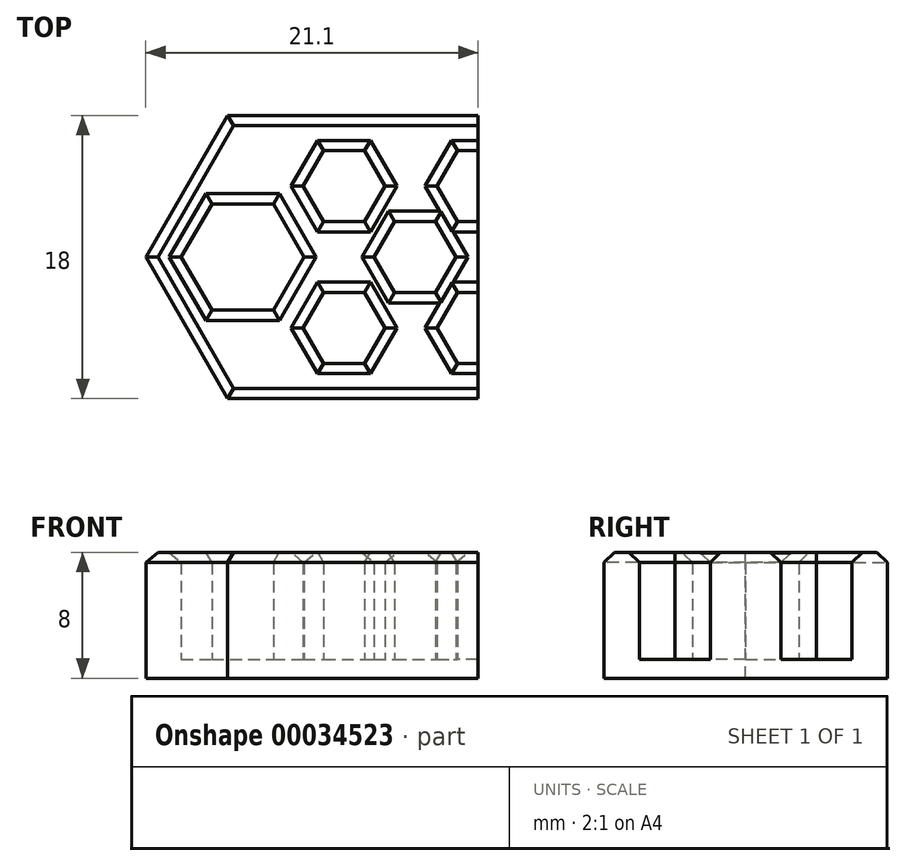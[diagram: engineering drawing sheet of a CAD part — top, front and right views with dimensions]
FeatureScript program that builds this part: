
annotation { "Feature Type Name" : "Feature", "Feature Type Description" : "" }
export const myFeature = defineFeature(function(context is Context, id is Id, definition is map)
    precondition{}
    {
        {
            assignVariable(context, id + "F0", {"name" : "d", "anyValue" : 4.5});
        }
        {
            var Q0;
            Q0=qCreatedBy(makeId("Top.planeOp"),FACE);
            var sketch = newSketch(context, id + "F1", { "sketchPlane" : qUnion([Q0])});
            skCircle(sketch, "E0.cCircle", {"center": v(0, 0) * mm, "radius": 2.25 * mm, "construction": true});
            skLineSegment(sketch, "E0.0", {"start": v(-1.3, 2.25) * mm, "end": v(1.3, 2.25) * mm});
            skLineSegment(sketch, "E0.1", {"start": v(1.3, 2.25) * mm, "end": v(2.6, 0) * mm});
            skLineSegment(sketch, "E0.2", {"start": v(2.6, 0) * mm, "end": v(1.3, -2.25) * mm});
            skLineSegment(sketch, "E0.3", {"start": v(1.3, -2.25) * mm, "end": v(-1.3, -2.25) * mm});
            skLineSegment(sketch, "E0.4", {"start": v(-1.3, -2.25) * mm, "end": v(-2.6, 0) * mm});
            skLineSegment(sketch, "E0.5", {"start": v(-2.6, 0) * mm, "end": v(-1.3, 2.25) * mm});
            skPoint(sketch, "E0.0.midPoint", {"position": v(0, 2.25) * mm});
            skCircle(sketch, "E1.cCircle", {"center": v(0, 9) * mm, "radius": 2.25 * mm, "construction": true});
            skLineSegment(sketch, "E1.0", {"start": v(-1.3, 11.25) * mm, "end": v(1.3, 11.25) * mm});
            skLineSegment(sketch, "E1.1", {"start": v(1.3, 11.25) * mm, "end": v(2.6, 9) * mm});
            skLineSegment(sketch, "E1.2", {"start": v(2.6, 9) * mm, "end": v(1.3, 6.75) * mm});
            skLineSegment(sketch, "E1.3", {"start": v(1.3, 6.75) * mm, "end": v(-1.3, 6.75) * mm});
            skLineSegment(sketch, "E1.4", {"start": v(-1.3, 6.75) * mm, "end": v(-2.6, 9) * mm});
            skLineSegment(sketch, "E1.5", {"start": v(-2.6, 9) * mm, "end": v(-1.3, 11.25) * mm});
            skPoint(sketch, "E1.0.midPoint", {"position": v(0, 11.25) * mm});
            skLineSegment(sketch, "E2", {"start": v(0, 0) * mm, "end": v(14.14, 14.14) * mm, "construction": true});
            skLineSegment(sketch, "E3", {"start": v(0, 2.25) * mm, "end": v(0, 6.75) * mm, "construction": true});
            skPoint(sketch, "E4", {"position": v(0, 4.5) * mm});
            skCircle(sketch, "E5.cCircle", {"center": v(4.5, 4.5) * mm, "radius": 2.25 * mm, "construction": true});
            skLineSegment(sketch, "E5.0", {"start": v(3.2, 6.75) * mm, "end": v(5.8, 6.75) * mm});
            skLineSegment(sketch, "E5.1", {"start": v(5.8, 6.75) * mm, "end": v(7.1, 4.5) * mm});
            skLineSegment(sketch, "E5.2", {"start": v(7.1, 4.5) * mm, "end": v(5.8, 2.25) * mm});
            skLineSegment(sketch, "E5.3", {"start": v(5.8, 2.25) * mm, "end": v(3.2, 2.25) * mm});
            skLineSegment(sketch, "E5.4", {"start": v(3.2, 2.25) * mm, "end": v(1.9, 4.5) * mm});
            skLineSegment(sketch, "E5.5", {"start": v(1.9, 4.5) * mm, "end": v(3.2, 6.75) * mm});
            skPoint(sketch, "E5.0.midPoint", {"position": v(4.5, 6.75) * mm});
            skCircle(sketch, "E6.1.0.0", {"center": v(13, 4.5) * mm, "radius": 2.25 * mm, "construction": true});
            skLineSegment(sketch, "E6.1.0.1", {"start": v(14.3, 6.75) * mm, "end": v(15.6, 4.5) * mm});
            skPoint(sketch, "E6.1.0.2", {"position": v(8.5, 2.25) * mm});
            skLineSegment(sketch, "E6.1.0.3", {"start": v(14.3, 2.25) * mm, "end": v(11.7, 2.25) * mm});
            skPoint(sketch, "E6.1.0.4", {"position": v(8.5, 11.25) * mm});
            skLineSegment(sketch, "E6.1.0.5", {"start": v(10.4, 4.5) * mm, "end": v(11.7, 6.75) * mm});
            skLineSegment(sketch, "E6.1.0.6", {"start": v(7.2, 6.75) * mm, "end": v(5.9, 9) * mm});
            skLineSegment(sketch, "E6.1.0.7", {"start": v(9.8, 6.75) * mm, "end": v(7.2, 6.75) * mm});
            skLineSegment(sketch, "E6.1.0.8", {"start": v(11.1, 9) * mm, "end": v(9.8, 6.75) * mm});
            skLineSegment(sketch, "E6.1.0.9", {"start": v(9.8, 11.25) * mm, "end": v(11.1, 9) * mm});
            skPoint(sketch, "E6.1.0.10", {"position": v(13, 6.75) * mm});
            skLineSegment(sketch, "E6.1.0.11", {"start": v(5.9, 9) * mm, "end": v(7.2, 11.25) * mm});
            skCircle(sketch, "E6.1.0.12", {"center": v(8.5, 9) * mm, "radius": 2.25 * mm, "construction": true});
            skLineSegment(sketch, "E6.1.0.13", {"start": v(15.6, 4.5) * mm, "end": v(14.3, 2.25) * mm});
            skLineSegment(sketch, "E6.1.0.14", {"start": v(11.7, 2.25) * mm, "end": v(10.4, 4.5) * mm});
            skLineSegment(sketch, "E6.1.0.15", {"start": v(5.9, 0) * mm, "end": v(7.2, 2.25) * mm});
            skLineSegment(sketch, "E6.1.0.16", {"start": v(7.2, -2.25) * mm, "end": v(5.9, 0) * mm});
            skLineSegment(sketch, "E6.1.0.17", {"start": v(9.8, -2.25) * mm, "end": v(7.2, -2.25) * mm});
            skLineSegment(sketch, "E6.1.0.18", {"start": v(11.1, 0) * mm, "end": v(9.8, -2.25) * mm});
            skLineSegment(sketch, "E6.1.0.19", {"start": v(9.8, 2.25) * mm, "end": v(11.1, 0) * mm});
            skCircle(sketch, "E6.1.0.20", {"center": v(8.5, 0) * mm, "radius": 2.25 * mm, "construction": true});
            skLineSegment(sketch, "E6.1.0.21", {"start": v(7.2, 11.25) * mm, "end": v(9.8, 11.25) * mm});
            skLineSegment(sketch, "E6.1.0.22", {"start": v(11.7, 6.75) * mm, "end": v(14.3, 6.75) * mm});
            skLineSegment(sketch, "E6.1.0.23", {"start": v(7.2, 2.25) * mm, "end": v(9.8, 2.25) * mm});
            skCircle(sketch, "E6.2.0.0", {"center": v(21.5, 4.5) * mm, "radius": 2.25 * mm, "construction": true});
            skLineSegment(sketch, "E6.2.0.1", {"start": v(22.8, 6.75) * mm, "end": v(24.1, 4.5) * mm});
            skPoint(sketch, "E6.2.0.2", {"position": v(17, 2.25) * mm});
            skLineSegment(sketch, "E6.2.0.3", {"start": v(22.8, 2.25) * mm, "end": v(20.2, 2.25) * mm});
            skPoint(sketch, "E6.2.0.4", {"position": v(17, 11.25) * mm});
            skLineSegment(sketch, "E6.2.0.5", {"start": v(18.9, 4.5) * mm, "end": v(20.2, 6.75) * mm});
            skLineSegment(sketch, "E6.2.0.6", {"start": v(15.7, 6.75) * mm, "end": v(14.4, 9) * mm});
            skLineSegment(sketch, "E6.2.0.7", {"start": v(18.3, 6.75) * mm, "end": v(15.7, 6.75) * mm});
            skLineSegment(sketch, "E6.2.0.8", {"start": v(19.6, 9) * mm, "end": v(18.3, 6.75) * mm});
            skLineSegment(sketch, "E6.2.0.9", {"start": v(18.3, 11.25) * mm, "end": v(19.6, 9) * mm});
            skPoint(sketch, "E6.2.0.10", {"position": v(21.5, 6.75) * mm});
            skLineSegment(sketch, "E6.2.0.11", {"start": v(14.4, 9) * mm, "end": v(15.7, 11.25) * mm});
            skCircle(sketch, "E6.2.0.12", {"center": v(17, 9) * mm, "radius": 2.25 * mm, "construction": true});
            skLineSegment(sketch, "E6.2.0.13", {"start": v(24.1, 4.5) * mm, "end": v(22.8, 2.25) * mm});
            skLineSegment(sketch, "E6.2.0.14", {"start": v(20.2, 2.25) * mm, "end": v(18.9, 4.5) * mm});
            skLineSegment(sketch, "E6.2.0.15", {"start": v(14.4, 0) * mm, "end": v(15.7, 2.25) * mm});
            skLineSegment(sketch, "E6.2.0.16", {"start": v(15.7, -2.25) * mm, "end": v(14.4, 0) * mm});
            skLineSegment(sketch, "E6.2.0.17", {"start": v(18.3, -2.25) * mm, "end": v(15.7, -2.25) * mm});
            skLineSegment(sketch, "E6.2.0.18", {"start": v(19.6, 0) * mm, "end": v(18.3, -2.25) * mm});
            skLineSegment(sketch, "E6.2.0.19", {"start": v(18.3, 2.25) * mm, "end": v(19.6, 0) * mm});
            skCircle(sketch, "E6.2.0.20", {"center": v(17, 0) * mm, "radius": 2.25 * mm, "construction": true});
            skLineSegment(sketch, "E6.2.0.21", {"start": v(15.7, 11.25) * mm, "end": v(18.3, 11.25) * mm});
            skLineSegment(sketch, "E6.2.0.22", {"start": v(20.2, 6.75) * mm, "end": v(22.8, 6.75) * mm});
            skLineSegment(sketch, "E6.2.0.23", {"start": v(15.7, 2.25) * mm, "end": v(18.3, 2.25) * mm});
            skCircle(sketch, "E6.3.0.0", {"center": v(30, 4.5) * mm, "radius": 2.25 * mm, "construction": true});
            skLineSegment(sketch, "E6.3.0.1", {"start": v(31.3, 6.75) * mm, "end": v(32.6, 4.5) * mm});
            skPoint(sketch, "E6.3.0.2", {"position": v(25.5, 2.25) * mm});
            skLineSegment(sketch, "E6.3.0.3", {"start": v(31.3, 2.25) * mm, "end": v(28.7, 2.25) * mm});
            skPoint(sketch, "E6.3.0.4", {"position": v(25.5, 11.25) * mm});
            skLineSegment(sketch, "E6.3.0.5", {"start": v(27.4, 4.5) * mm, "end": v(28.7, 6.75) * mm});
            skLineSegment(sketch, "E6.3.0.6", {"start": v(24.2, 6.75) * mm, "end": v(22.9, 9) * mm});
            skLineSegment(sketch, "E6.3.0.7", {"start": v(26.8, 6.75) * mm, "end": v(24.2, 6.75) * mm});
            skLineSegment(sketch, "E6.3.0.8", {"start": v(28.1, 9) * mm, "end": v(26.8, 6.75) * mm});
            skLineSegment(sketch, "E6.3.0.9", {"start": v(26.8, 11.25) * mm, "end": v(28.1, 9) * mm});
            skPoint(sketch, "E6.3.0.10", {"position": v(30, 6.75) * mm});
            skLineSegment(sketch, "E6.3.0.11", {"start": v(22.9, 9) * mm, "end": v(24.2, 11.25) * mm});
            skCircle(sketch, "E6.3.0.12", {"center": v(25.5, 9) * mm, "radius": 2.25 * mm, "construction": true});
            skLineSegment(sketch, "E6.3.0.13", {"start": v(32.6, 4.5) * mm, "end": v(31.3, 2.25) * mm});
            skLineSegment(sketch, "E6.3.0.14", {"start": v(28.7, 2.25) * mm, "end": v(27.4, 4.5) * mm});
            skLineSegment(sketch, "E6.3.0.15", {"start": v(22.9, 0) * mm, "end": v(24.2, 2.25) * mm});
            skLineSegment(sketch, "E6.3.0.16", {"start": v(24.2, -2.25) * mm, "end": v(22.9, 0) * mm});
            skLineSegment(sketch, "E6.3.0.17", {"start": v(26.8, -2.25) * mm, "end": v(24.2, -2.25) * mm});
            skLineSegment(sketch, "E6.3.0.18", {"start": v(28.1, 0) * mm, "end": v(26.8, -2.25) * mm});
            skLineSegment(sketch, "E6.3.0.19", {"start": v(26.8, 2.25) * mm, "end": v(28.1, 0) * mm});
            skCircle(sketch, "E6.3.0.20", {"center": v(25.5, 0) * mm, "radius": 2.25 * mm, "construction": true});
            skLineSegment(sketch, "E6.3.0.21", {"start": v(24.2, 11.25) * mm, "end": v(26.8, 11.25) * mm});
            skLineSegment(sketch, "E6.3.0.22", {"start": v(28.7, 6.75) * mm, "end": v(31.3, 6.75) * mm});
            skLineSegment(sketch, "E6.3.0.23", {"start": v(24.2, 2.25) * mm, "end": v(26.8, 2.25) * mm});
            skCircle(sketch, "E6.4.0.0", {"center": v(38.5, 4.5) * mm, "radius": 2.25 * mm, "construction": true});
            skLineSegment(sketch, "E6.4.0.1", {"start": v(39.8, 6.75) * mm, "end": v(41.1, 4.5) * mm});
            skPoint(sketch, "E6.4.0.2", {"position": v(34, 2.25) * mm});
            skLineSegment(sketch, "E6.4.0.3", {"start": v(39.8, 2.25) * mm, "end": v(37.2, 2.25) * mm});
            skPoint(sketch, "E6.4.0.4", {"position": v(34, 11.25) * mm});
            skLineSegment(sketch, "E6.4.0.5", {"start": v(35.9, 4.5) * mm, "end": v(37.2, 6.75) * mm});
            skLineSegment(sketch, "E6.4.0.6", {"start": v(32.7, 6.75) * mm, "end": v(31.4, 9) * mm});
            skLineSegment(sketch, "E6.4.0.7", {"start": v(35.3, 6.75) * mm, "end": v(32.7, 6.75) * mm});
            skLineSegment(sketch, "E6.4.0.8", {"start": v(36.6, 9) * mm, "end": v(35.3, 6.75) * mm});
            skLineSegment(sketch, "E6.4.0.9", {"start": v(35.3, 11.25) * mm, "end": v(36.6, 9) * mm});
            skPoint(sketch, "E6.4.0.10", {"position": v(38.5, 6.75) * mm});
            skLineSegment(sketch, "E6.4.0.11", {"start": v(31.4, 9) * mm, "end": v(32.7, 11.25) * mm});
            skCircle(sketch, "E6.4.0.12", {"center": v(34, 9) * mm, "radius": 2.25 * mm, "construction": true});
            skLineSegment(sketch, "E6.4.0.13", {"start": v(41.1, 4.5) * mm, "end": v(39.8, 2.25) * mm});
            skLineSegment(sketch, "E6.4.0.14", {"start": v(37.2, 2.25) * mm, "end": v(35.9, 4.5) * mm});
            skLineSegment(sketch, "E6.4.0.15", {"start": v(31.4, 0) * mm, "end": v(32.7, 2.25) * mm});
            skLineSegment(sketch, "E6.4.0.16", {"start": v(32.7, -2.25) * mm, "end": v(31.4, 0) * mm});
            skLineSegment(sketch, "E6.4.0.17", {"start": v(35.3, -2.25) * mm, "end": v(32.7, -2.25) * mm});
            skLineSegment(sketch, "E6.4.0.18", {"start": v(36.6, 0) * mm, "end": v(35.3, -2.25) * mm});
            skLineSegment(sketch, "E6.4.0.19", {"start": v(35.3, 2.25) * mm, "end": v(36.6, 0) * mm});
            skCircle(sketch, "E6.4.0.20", {"center": v(34, 0) * mm, "radius": 2.25 * mm, "construction": true});
            skLineSegment(sketch, "E6.4.0.21", {"start": v(32.7, 11.25) * mm, "end": v(35.3, 11.25) * mm});
            skLineSegment(sketch, "E6.4.0.22", {"start": v(37.2, 6.75) * mm, "end": v(39.8, 6.75) * mm});
            skLineSegment(sketch, "E6.4.0.23", {"start": v(32.7, 2.25) * mm, "end": v(35.3, 2.25) * mm});
            skCircle(sketch, "E6.5.0.0", {"center": v(47, 4.5) * mm, "radius": 2.25 * mm, "construction": true});
            skLineSegment(sketch, "E6.5.0.1", {"start": v(48.3, 6.75) * mm, "end": v(49.6, 4.5) * mm});
            skPoint(sketch, "E6.5.0.2", {"position": v(42.5, 2.25) * mm});
            skLineSegment(sketch, "E6.5.0.3", {"start": v(48.3, 2.25) * mm, "end": v(45.7, 2.25) * mm});
            skPoint(sketch, "E6.5.0.4", {"position": v(42.5, 11.25) * mm});
            skLineSegment(sketch, "E6.5.0.5", {"start": v(44.4, 4.5) * mm, "end": v(45.7, 6.75) * mm});
            skLineSegment(sketch, "E6.5.0.6", {"start": v(41.2, 6.75) * mm, "end": v(39.9, 9) * mm});
            skLineSegment(sketch, "E6.5.0.7", {"start": v(43.8, 6.75) * mm, "end": v(41.2, 6.75) * mm});
            skLineSegment(sketch, "E6.5.0.8", {"start": v(45.1, 9) * mm, "end": v(43.8, 6.75) * mm});
            skLineSegment(sketch, "E6.5.0.9", {"start": v(43.8, 11.25) * mm, "end": v(45.1, 9) * mm});
            skPoint(sketch, "E6.5.0.10", {"position": v(47, 6.75) * mm});
            skLineSegment(sketch, "E6.5.0.11", {"start": v(39.9, 9) * mm, "end": v(41.2, 11.25) * mm});
            skCircle(sketch, "E6.5.0.12", {"center": v(42.5, 9) * mm, "radius": 2.25 * mm, "construction": true});
            skLineSegment(sketch, "E6.5.0.13", {"start": v(49.6, 4.5) * mm, "end": v(48.3, 2.25) * mm});
            skLineSegment(sketch, "E6.5.0.14", {"start": v(45.7, 2.25) * mm, "end": v(44.4, 4.5) * mm});
            skLineSegment(sketch, "E6.5.0.15", {"start": v(39.9, 0) * mm, "end": v(41.2, 2.25) * mm});
            skLineSegment(sketch, "E6.5.0.16", {"start": v(41.2, -2.25) * mm, "end": v(39.9, 0) * mm});
            skLineSegment(sketch, "E6.5.0.17", {"start": v(43.8, -2.25) * mm, "end": v(41.2, -2.25) * mm});
            skLineSegment(sketch, "E6.5.0.18", {"start": v(45.1, 0) * mm, "end": v(43.8, -2.25) * mm});
            skLineSegment(sketch, "E6.5.0.19", {"start": v(43.8, 2.25) * mm, "end": v(45.1, 0) * mm});
            skCircle(sketch, "E6.5.0.20", {"center": v(42.5, 0) * mm, "radius": 2.25 * mm, "construction": true});
            skLineSegment(sketch, "E6.5.0.21", {"start": v(41.2, 11.25) * mm, "end": v(43.8, 11.25) * mm});
            skLineSegment(sketch, "E6.5.0.22", {"start": v(45.7, 6.75) * mm, "end": v(48.3, 6.75) * mm});
            skLineSegment(sketch, "E6.5.0.23", {"start": v(41.2, 2.25) * mm, "end": v(43.8, 2.25) * mm});
            skCircle(sketch, "E6.6.0.0", {"center": v(55.5, 4.5) * mm, "radius": 2.25 * mm, "construction": true});
            skLineSegment(sketch, "E6.6.0.1", {"start": v(56.8, 6.75) * mm, "end": v(58.1, 4.5) * mm});
            skPoint(sketch, "E6.6.0.2", {"position": v(51, 2.25) * mm});
            skLineSegment(sketch, "E6.6.0.3", {"start": v(56.8, 2.25) * mm, "end": v(54.2, 2.25) * mm});
            skPoint(sketch, "E6.6.0.4", {"position": v(51, 11.25) * mm});
            skLineSegment(sketch, "E6.6.0.5", {"start": v(52.9, 4.5) * mm, "end": v(54.2, 6.75) * mm});
            skLineSegment(sketch, "E6.6.0.6", {"start": v(49.7, 6.75) * mm, "end": v(48.4, 9) * mm});
            skLineSegment(sketch, "E6.6.0.7", {"start": v(52.3, 6.75) * mm, "end": v(49.7, 6.75) * mm});
            skLineSegment(sketch, "E6.6.0.8", {"start": v(53.6, 9) * mm, "end": v(52.3, 6.75) * mm});
            skLineSegment(sketch, "E6.6.0.9", {"start": v(52.3, 11.25) * mm, "end": v(53.6, 9) * mm});
            skPoint(sketch, "E6.6.0.10", {"position": v(55.5, 6.75) * mm});
            skLineSegment(sketch, "E6.6.0.11", {"start": v(48.4, 9) * mm, "end": v(49.7, 11.25) * mm});
            skCircle(sketch, "E6.6.0.12", {"center": v(51, 9) * mm, "radius": 2.25 * mm, "construction": true});
            skLineSegment(sketch, "E6.6.0.13", {"start": v(58.1, 4.5) * mm, "end": v(56.8, 2.25) * mm});
            skLineSegment(sketch, "E6.6.0.14", {"start": v(54.2, 2.25) * mm, "end": v(52.9, 4.5) * mm});
            skLineSegment(sketch, "E6.6.0.15", {"start": v(48.4, 0) * mm, "end": v(49.7, 2.25) * mm});
            skLineSegment(sketch, "E6.6.0.16", {"start": v(49.7, -2.25) * mm, "end": v(48.4, 0) * mm});
            skLineSegment(sketch, "E6.6.0.17", {"start": v(52.3, -2.25) * mm, "end": v(49.7, -2.25) * mm});
            skLineSegment(sketch, "E6.6.0.18", {"start": v(53.6, 0) * mm, "end": v(52.3, -2.25) * mm});
            skLineSegment(sketch, "E6.6.0.19", {"start": v(52.3, 2.25) * mm, "end": v(53.6, 0) * mm});
            skCircle(sketch, "E6.6.0.20", {"center": v(51, 0) * mm, "radius": 2.25 * mm, "construction": true});
            skLineSegment(sketch, "E6.6.0.21", {"start": v(49.7, 11.25) * mm, "end": v(52.3, 11.25) * mm});
            skLineSegment(sketch, "E6.6.0.22", {"start": v(54.2, 6.75) * mm, "end": v(56.8, 6.75) * mm});
            skLineSegment(sketch, "E6.6.0.23", {"start": v(49.7, 2.25) * mm, "end": v(52.3, 2.25) * mm});
            skCircle(sketch, "E6.7.0.0", {"center": v(64, 4.5) * mm, "radius": 2.25 * mm, "construction": true});
            skLineSegment(sketch, "E6.7.0.1", {"start": v(65.3, 6.75) * mm, "end": v(66.6, 4.5) * mm});
            skPoint(sketch, "E6.7.0.2", {"position": v(59.5, 2.25) * mm});
            skLineSegment(sketch, "E6.7.0.3", {"start": v(65.3, 2.25) * mm, "end": v(62.7, 2.25) * mm});
            skPoint(sketch, "E6.7.0.4", {"position": v(59.5, 11.25) * mm});
            skLineSegment(sketch, "E6.7.0.5", {"start": v(61.4, 4.5) * mm, "end": v(62.7, 6.75) * mm});
            skLineSegment(sketch, "E6.7.0.6", {"start": v(58.2, 6.75) * mm, "end": v(56.9, 9) * mm});
            skLineSegment(sketch, "E6.7.0.7", {"start": v(60.8, 6.75) * mm, "end": v(58.2, 6.75) * mm});
            skLineSegment(sketch, "E6.7.0.8", {"start": v(62.1, 9) * mm, "end": v(60.8, 6.75) * mm});
            skLineSegment(sketch, "E6.7.0.9", {"start": v(60.8, 11.25) * mm, "end": v(62.1, 9) * mm});
            skPoint(sketch, "E6.7.0.10", {"position": v(64, 6.75) * mm});
            skLineSegment(sketch, "E6.7.0.11", {"start": v(56.9, 9) * mm, "end": v(58.2, 11.25) * mm});
            skCircle(sketch, "E6.7.0.12", {"center": v(59.5, 9) * mm, "radius": 2.25 * mm, "construction": true});
            skLineSegment(sketch, "E6.7.0.13", {"start": v(66.6, 4.5) * mm, "end": v(65.3, 2.25) * mm});
            skLineSegment(sketch, "E6.7.0.14", {"start": v(62.7, 2.25) * mm, "end": v(61.4, 4.5) * mm});
            skLineSegment(sketch, "E6.7.0.15", {"start": v(56.9, 0) * mm, "end": v(58.2, 2.25) * mm});
            skLineSegment(sketch, "E6.7.0.16", {"start": v(58.2, -2.25) * mm, "end": v(56.9, 0) * mm});
            skLineSegment(sketch, "E6.7.0.17", {"start": v(60.8, -2.25) * mm, "end": v(58.2, -2.25) * mm});
            skLineSegment(sketch, "E6.7.0.18", {"start": v(62.1, 0) * mm, "end": v(60.8, -2.25) * mm});
            skLineSegment(sketch, "E6.7.0.19", {"start": v(60.8, 2.25) * mm, "end": v(62.1, 0) * mm});
            skCircle(sketch, "E6.7.0.20", {"center": v(59.5, 0) * mm, "radius": 2.25 * mm, "construction": true});
            skLineSegment(sketch, "E6.7.0.21", {"start": v(58.2, 11.25) * mm, "end": v(60.8, 11.25) * mm});
            skLineSegment(sketch, "E6.7.0.22", {"start": v(62.7, 6.75) * mm, "end": v(65.3, 6.75) * mm});
            skLineSegment(sketch, "E6.7.0.23", {"start": v(58.2, 2.25) * mm, "end": v(60.8, 2.25) * mm});
            skCircle(sketch, "E6.8.0.0", {"center": v(72.5, 4.5) * mm, "radius": 2.25 * mm, "construction": true});
            skLineSegment(sketch, "E6.8.0.1", {"start": v(73.8, 6.75) * mm, "end": v(75.1, 4.5) * mm});
            skPoint(sketch, "E6.8.0.2", {"position": v(68, 2.25) * mm});
            skLineSegment(sketch, "E6.8.0.3", {"start": v(73.8, 2.25) * mm, "end": v(71.2, 2.25) * mm});
            skPoint(sketch, "E6.8.0.4", {"position": v(68, 11.25) * mm});
            skLineSegment(sketch, "E6.8.0.5", {"start": v(69.9, 4.5) * mm, "end": v(71.2, 6.75) * mm});
            skLineSegment(sketch, "E6.8.0.6", {"start": v(66.7, 6.75) * mm, "end": v(65.4, 9) * mm});
            skLineSegment(sketch, "E6.8.0.7", {"start": v(69.3, 6.75) * mm, "end": v(66.7, 6.75) * mm});
            skLineSegment(sketch, "E6.8.0.8", {"start": v(70.6, 9) * mm, "end": v(69.3, 6.75) * mm});
            skLineSegment(sketch, "E6.8.0.9", {"start": v(69.3, 11.25) * mm, "end": v(70.6, 9) * mm});
            skPoint(sketch, "E6.8.0.10", {"position": v(72.5, 6.75) * mm});
            skLineSegment(sketch, "E6.8.0.11", {"start": v(65.4, 9) * mm, "end": v(66.7, 11.25) * mm});
            skCircle(sketch, "E6.8.0.12", {"center": v(68, 9) * mm, "radius": 2.25 * mm, "construction": true});
            skLineSegment(sketch, "E6.8.0.13", {"start": v(75.1, 4.5) * mm, "end": v(73.8, 2.25) * mm});
            skLineSegment(sketch, "E6.8.0.14", {"start": v(71.2, 2.25) * mm, "end": v(69.9, 4.5) * mm});
            skLineSegment(sketch, "E6.8.0.15", {"start": v(65.4, 0) * mm, "end": v(66.7, 2.25) * mm});
            skLineSegment(sketch, "E6.8.0.16", {"start": v(66.7, -2.25) * mm, "end": v(65.4, 0) * mm});
            skLineSegment(sketch, "E6.8.0.17", {"start": v(69.3, -2.25) * mm, "end": v(66.7, -2.25) * mm});
            skLineSegment(sketch, "E6.8.0.18", {"start": v(70.6, 0) * mm, "end": v(69.3, -2.25) * mm});
            skLineSegment(sketch, "E6.8.0.19", {"start": v(69.3, 2.25) * mm, "end": v(70.6, 0) * mm});
            skCircle(sketch, "E6.8.0.20", {"center": v(68, 0) * mm, "radius": 2.25 * mm, "construction": true});
            skLineSegment(sketch, "E6.8.0.21", {"start": v(66.7, 11.25) * mm, "end": v(69.3, 11.25) * mm});
            skLineSegment(sketch, "E6.8.0.22", {"start": v(71.2, 6.75) * mm, "end": v(73.8, 6.75) * mm});
            skLineSegment(sketch, "E6.8.0.23", {"start": v(66.7, 2.25) * mm, "end": v(69.3, 2.25) * mm});
            skCircle(sketch, "E6.9.0.0", {"center": v(81, 4.5) * mm, "radius": 2.25 * mm, "construction": true});
            skLineSegment(sketch, "E6.9.0.1", {"start": v(82.3, 6.75) * mm, "end": v(83.6, 4.5) * mm});
            skPoint(sketch, "E6.9.0.2", {"position": v(76.5, 2.25) * mm});
            skLineSegment(sketch, "E6.9.0.3", {"start": v(82.3, 2.25) * mm, "end": v(79.7, 2.25) * mm});
            skPoint(sketch, "E6.9.0.4", {"position": v(76.5, 11.25) * mm});
            skLineSegment(sketch, "E6.9.0.5", {"start": v(78.4, 4.5) * mm, "end": v(79.7, 6.75) * mm});
            skLineSegment(sketch, "E6.9.0.6", {"start": v(75.2, 6.75) * mm, "end": v(73.9, 9) * mm});
            skLineSegment(sketch, "E6.9.0.7", {"start": v(77.8, 6.75) * mm, "end": v(75.2, 6.75) * mm});
            skLineSegment(sketch, "E6.9.0.8", {"start": v(79.1, 9) * mm, "end": v(77.8, 6.75) * mm});
            skLineSegment(sketch, "E6.9.0.9", {"start": v(77.8, 11.25) * mm, "end": v(79.1, 9) * mm});
            skPoint(sketch, "E6.9.0.10", {"position": v(81, 6.75) * mm});
            skLineSegment(sketch, "E6.9.0.11", {"start": v(73.9, 9) * mm, "end": v(75.2, 11.25) * mm});
            skCircle(sketch, "E6.9.0.12", {"center": v(76.5, 9) * mm, "radius": 2.25 * mm, "construction": true});
            skLineSegment(sketch, "E6.9.0.13", {"start": v(83.6, 4.5) * mm, "end": v(82.3, 2.25) * mm});
            skLineSegment(sketch, "E6.9.0.14", {"start": v(79.7, 2.25) * mm, "end": v(78.4, 4.5) * mm});
            skLineSegment(sketch, "E6.9.0.15", {"start": v(73.9, 0) * mm, "end": v(75.2, 2.25) * mm});
            skLineSegment(sketch, "E6.9.0.16", {"start": v(75.2, -2.25) * mm, "end": v(73.9, 0) * mm});
            skLineSegment(sketch, "E6.9.0.17", {"start": v(77.8, -2.25) * mm, "end": v(75.2, -2.25) * mm});
            skLineSegment(sketch, "E6.9.0.18", {"start": v(79.1, 0) * mm, "end": v(77.8, -2.25) * mm});
            skLineSegment(sketch, "E6.9.0.19", {"start": v(77.8, 2.25) * mm, "end": v(79.1, 0) * mm});
            skCircle(sketch, "E6.9.0.20", {"center": v(76.5, 0) * mm, "radius": 2.25 * mm, "construction": true});
            skLineSegment(sketch, "E6.9.0.21", {"start": v(75.2, 11.25) * mm, "end": v(77.8, 11.25) * mm});
            skLineSegment(sketch, "E6.9.0.22", {"start": v(79.7, 6.75) * mm, "end": v(82.3, 6.75) * mm});
            skLineSegment(sketch, "E6.9.0.23", {"start": v(75.2, 2.25) * mm, "end": v(77.8, 2.25) * mm});
            skLineSegment(sketch, "E6.direction1", {"start": v(4.5, 4.5) * mm, "end": v(13, 4.5) * mm, "construction": true});
            skLineSegment(sketch, "E7.bottom", {"start": v(-12.6, 13.5) * mm, "end": v(85.85, 13.5) * mm});
            skLineSegment(sketch, "E7.top", {"start": v(-12.6, -4.5) * mm, "end": v(85.85, -4.5) * mm});
            skLineSegment(sketch, "E7.left", {"start": v(-12.6, 13.5) * mm, "end": v(-12.6, -4.5) * mm});
            skLineSegment(sketch, "E7.right", {"start": v(85.85, 13.5) * mm, "end": v(85.85, -4.5) * mm});
            skCircle(sketch, "E8.cCircle", {"center": v(-6.45, 4.5) * mm, "radius": 3.37 * mm, "construction": true});
            skLineSegment(sketch, "E8.0", {"start": v(-8.4, 7.87) * mm, "end": v(-4.5, 7.87) * mm});
            skLineSegment(sketch, "E8.1", {"start": v(-4.5, 7.87) * mm, "end": v(-2.55, 4.5) * mm});
            skLineSegment(sketch, "E8.2", {"start": v(-2.55, 4.5) * mm, "end": v(-4.5, 1.12) * mm});
            skLineSegment(sketch, "E8.3", {"start": v(-4.5, 1.12) * mm, "end": v(-8.4, 1.12) * mm});
            skLineSegment(sketch, "E8.4", {"start": v(-8.4, 1.12) * mm, "end": v(-10.35, 4.5) * mm});
            skLineSegment(sketch, "E8.5", {"start": v(-10.35, 4.5) * mm, "end": v(-8.4, 7.88) * mm});
            skPoint(sketch, "E8.0.midPoint", {"position": v(-6.45, 7.88) * mm});
            skLineSegment(sketch, "E9", {"start": v(-4.5, 7.87) * mm, "end": v(-2.6, 7.87) * mm, "construction": true});
            skLineSegment(sketch, "E10", {"start": v(1.3, 6.75) * mm, "end": v(3.2, 6.75) * mm, "construction": true});
            skSolve(sketch);
        }
        {
            var Q0;
            Q0=makeQuery(id+"F1.imprint","IMPRINT",FACE,{"disambiguationData":[TD([[makeQuery(id+"F1.imprint","IMPRINT",EDGE,{"derivedFrom":sQuery(id+"F1.wireOp",EDGE,"E0.0")}),1.0]])]});
            extrude(context, id + "F2", {"entities" : qUnion([Q0]), "depth" : 8 * mm});
        }
        {
            var Q0;
            Q0=makeQuery(id+"F1.imprint","IMPRINT",FACE,{"disambiguationData":[TD([[makeQuery(id+"F1.imprint","IMPRINT",EDGE,{"derivedFrom":sQuery(id+"F1.wireOp",EDGE,"E0.0")}),1.0]])]});
            var sketch = newSketch(context, id + "F3", { "sketchPlane" : qUnion([Q0])});
            skPoint(sketch, "E11.0", {"position": v(-12.6, -4.5) * mm});
            skPoint(sketch, "E12.0", {"position": v(85.85, 13.5) * mm});
            skLineSegment(sketch, "E13.bottom", {"start": v(-12.6, -4.5) * mm, "end": v(85.85, -4.5) * mm});
            skLineSegment(sketch, "E13.top", {"start": v(-12.6, 13.5) * mm, "end": v(85.85, 13.5) * mm});
            skLineSegment(sketch, "E13.left", {"start": v(-12.6, -4.5) * mm, "end": v(-12.6, 13.5) * mm});
            skLineSegment(sketch, "E13.right", {"start": v(85.85, -4.5) * mm, "end": v(85.85, 13.5) * mm});
            skSolve(sketch);
        }
        {
            var Q0;
            Q0 = qSketchRegion(id + "F3", true);
            extrude(context, id + "F4", {"entities" : qUnion([Q0]), "operationType" : NewBodyOperationType.ADD, "depth" : 1.2 * mm});
        }
        {
            var Q0;
            Q0=makeQuery(id+"F2.opExtrude","SWEPT_EDGE",EDGE,{"disambiguationData":[OSD([sQuery(id+"F1.wireOp",EDGE,"E7.top"),sQuery(id+"F1.wireOp",EDGE,"E7.left")])]});
            var Q1;
            Q1=makeQuery(id+"F2.opExtrude","SWEPT_EDGE",EDGE,{"disambiguationData":[OSD([sQuery(id+"F1.wireOp",EDGE,"E7.bottom"),sQuery(id+"F1.wireOp",EDGE,"E7.left")])]});
            var Q2;
            Q2=makeQuery(id+"F2.opExtrude","SWEPT_EDGE",EDGE,{"disambiguationData":[OSD([sQuery(id+"F1.wireOp",EDGE,"E7.top"),sQuery(id+"F1.wireOp",EDGE,"E7.right")])]});
            var Q3;
            Q3=makeQuery(id+"F2.opExtrude","SWEPT_EDGE",EDGE,{"disambiguationData":[OSD([sQuery(id+"F1.wireOp",EDGE,"E7.bottom"),sQuery(id+"F1.wireOp",EDGE,"E7.right")])]});
            chamfer(context, id + "F5", {"entities" : qUnion([Q0, Q1, Q2, Q3]), "chamferType" : ChamferType.OFFSET_ANGLE, "width" : (2 * getVariable(context, 'd') / tan(60 * degree)) * mm, "oppositeDirection" : false, "angle" : 60 * degree, "tangentPropagation" : true});
        }
        {
            var Q0;
            Q0=makeQuery(id+"F2.opExtrude","CAP_FACE",FACE,{"disambiguationData":[OSD([sQuery(id+"F1.wireOp",EDGE,"E0.0"),sQuery(id+"F1.wireOp",EDGE,"E0.1"),sQuery(id+"F1.wireOp",EDGE,"E0.2"),sQuery(id+"F1.wireOp",EDGE,"E0.3"),sQuery(id+"F1.wireOp",EDGE,"E0.4"),sQuery(id+"F1.wireOp",EDGE,"E0.5"),sQuery(id+"F1.wireOp",EDGE,"E1.0"),sQuery(id+"F1.wireOp",EDGE,"E1.1"),sQuery(id+"F1.wireOp",EDGE,"E1.2"),sQuery(id+"F1.wireOp",EDGE,"E1.3"),sQuery(id+"F1.wireOp",EDGE,"E1.4"),sQuery(id+"F1.wireOp",EDGE,"E1.5"),sQuery(id+"F1.wireOp",EDGE,"E5.0"),sQuery(id+"F1.wireOp",EDGE,"E5.1"),sQuery(id+"F1.wireOp",EDGE,"E5.2"),sQuery(id+"F1.wireOp",EDGE,"E5.3"),sQuery(id+"F1.wireOp",EDGE,"E5.4"),sQuery(id+"F1.wireOp",EDGE,"E5.5"),sQuery(id+"F1.wireOp",EDGE,"E6.1.0.1"),sQuery(id+"F1.wireOp",EDGE,"E6.1.0.3"),sQuery(id+"F1.wireOp",EDGE,"E6.1.0.5"),sQuery(id+"F1.wireOp",EDGE,"E6.1.0.6"),sQuery(id+"F1.wireOp",EDGE,"E6.1.0.7"),sQuery(id+"F1.wireOp",EDGE,"E6.1.0.8"),sQuery(id+"F1.wireOp",EDGE,"E6.1.0.9"),sQuery(id+"F1.wireOp",EDGE,"E6.1.0.11"),sQuery(id+"F1.wireOp",EDGE,"E6.1.0.13"),sQuery(id+"F1.wireOp",EDGE,"E6.1.0.14"),sQuery(id+"F1.wireOp",EDGE,"E6.1.0.15"),sQuery(id+"F1.wireOp",EDGE,"E6.1.0.16"),sQuery(id+"F1.wireOp",EDGE,"E6.1.0.17"),sQuery(id+"F1.wireOp",EDGE,"E6.1.0.18"),sQuery(id+"F1.wireOp",EDGE,"E6.1.0.19"),sQuery(id+"F1.wireOp",EDGE,"E6.1.0.21"),sQuery(id+"F1.wireOp",EDGE,"E6.1.0.22"),sQuery(id+"F1.wireOp",EDGE,"E6.1.0.23"),sQuery(id+"F1.wireOp",EDGE,"E6.2.0.1"),sQuery(id+"F1.wireOp",EDGE,"E6.2.0.3"),sQuery(id+"F1.wireOp",EDGE,"E6.2.0.5"),sQuery(id+"F1.wireOp",EDGE,"E6.2.0.6"),sQuery(id+"F1.wireOp",EDGE,"E6.2.0.7"),sQuery(id+"F1.wireOp",EDGE,"E6.2.0.8"),sQuery(id+"F1.wireOp",EDGE,"E6.2.0.9"),sQuery(id+"F1.wireOp",EDGE,"E6.2.0.11"),sQuery(id+"F1.wireOp",EDGE,"E6.2.0.13"),sQuery(id+"F1.wireOp",EDGE,"E6.2.0.14"),sQuery(id+"F1.wireOp",EDGE,"E6.2.0.15"),sQuery(id+"F1.wireOp",EDGE,"E6.2.0.16"),sQuery(id+"F1.wireOp",EDGE,"E6.2.0.17"),sQuery(id+"F1.wireOp",EDGE,"E6.2.0.18"),sQuery(id+"F1.wireOp",EDGE,"E6.2.0.19"),sQuery(id+"F1.wireOp",EDGE,"E6.2.0.21"),sQuery(id+"F1.wireOp",EDGE,"E6.2.0.22"),sQuery(id+"F1.wireOp",EDGE,"E6.2.0.23"),sQuery(id+"F1.wireOp",EDGE,"E6.3.0.1"),sQuery(id+"F1.wireOp",EDGE,"E6.3.0.3"),sQuery(id+"F1.wireOp",EDGE,"E6.3.0.5"),sQuery(id+"F1.wireOp",EDGE,"E6.3.0.6"),sQuery(id+"F1.wireOp",EDGE,"E6.3.0.7"),sQuery(id+"F1.wireOp",EDGE,"E6.3.0.8"),sQuery(id+"F1.wireOp",EDGE,"E6.3.0.9"),sQuery(id+"F1.wireOp",EDGE,"E6.3.0.11"),sQuery(id+"F1.wireOp",EDGE,"E6.3.0.13"),sQuery(id+"F1.wireOp",EDGE,"E6.3.0.14"),sQuery(id+"F1.wireOp",EDGE,"E6.3.0.15"),sQuery(id+"F1.wireOp",EDGE,"E6.3.0.16"),sQuery(id+"F1.wireOp",EDGE,"E6.3.0.17"),sQuery(id+"F1.wireOp",EDGE,"E6.3.0.18"),sQuery(id+"F1.wireOp",EDGE,"E6.3.0.19"),sQuery(id+"F1.wireOp",EDGE,"E6.3.0.21"),sQuery(id+"F1.wireOp",EDGE,"E6.3.0.22"),sQuery(id+"F1.wireOp",EDGE,"E6.3.0.23"),sQuery(id+"F1.wireOp",EDGE,"E6.4.0.1"),sQuery(id+"F1.wireOp",EDGE,"E6.4.0.3"),sQuery(id+"F1.wireOp",EDGE,"E6.4.0.5"),sQuery(id+"F1.wireOp",EDGE,"E6.4.0.6"),sQuery(id+"F1.wireOp",EDGE,"E6.4.0.7"),sQuery(id+"F1.wireOp",EDGE,"E6.4.0.8"),sQuery(id+"F1.wireOp",EDGE,"E6.4.0.9"),sQuery(id+"F1.wireOp",EDGE,"E6.4.0.11"),sQuery(id+"F1.wireOp",EDGE,"E6.4.0.13"),sQuery(id+"F1.wireOp",EDGE,"E6.4.0.14"),sQuery(id+"F1.wireOp",EDGE,"E6.4.0.15"),sQuery(id+"F1.wireOp",EDGE,"E6.4.0.16"),sQuery(id+"F1.wireOp",EDGE,"E6.4.0.17"),sQuery(id+"F1.wireOp",EDGE,"E6.4.0.18"),sQuery(id+"F1.wireOp",EDGE,"E6.4.0.19"),sQuery(id+"F1.wireOp",EDGE,"E6.4.0.21"),sQuery(id+"F1.wireOp",EDGE,"E6.4.0.22"),sQuery(id+"F1.wireOp",EDGE,"E6.4.0.23"),sQuery(id+"F1.wireOp",EDGE,"E6.5.0.1"),sQuery(id+"F1.wireOp",EDGE,"E6.5.0.3"),sQuery(id+"F1.wireOp",EDGE,"E6.5.0.5"),sQuery(id+"F1.wireOp",EDGE,"E6.5.0.6"),sQuery(id+"F1.wireOp",EDGE,"E6.5.0.7"),sQuery(id+"F1.wireOp",EDGE,"E6.5.0.8"),sQuery(id+"F1.wireOp",EDGE,"E6.5.0.9"),sQuery(id+"F1.wireOp",EDGE,"E6.5.0.11"),sQuery(id+"F1.wireOp",EDGE,"E6.5.0.13"),sQuery(id+"F1.wireOp",EDGE,"E6.5.0.14"),sQuery(id+"F1.wireOp",EDGE,"E6.5.0.15"),sQuery(id+"F1.wireOp",EDGE,"E6.5.0.16"),sQuery(id+"F1.wireOp",EDGE,"E6.5.0.17"),sQuery(id+"F1.wireOp",EDGE,"E6.5.0.18"),sQuery(id+"F1.wireOp",EDGE,"E6.5.0.19"),sQuery(id+"F1.wireOp",EDGE,"E6.5.0.21"),sQuery(id+"F1.wireOp",EDGE,"E6.5.0.22"),sQuery(id+"F1.wireOp",EDGE,"E6.5.0.23"),sQuery(id+"F1.wireOp",EDGE,"E6.6.0.1"),sQuery(id+"F1.wireOp",EDGE,"E6.6.0.3"),sQuery(id+"F1.wireOp",EDGE,"E6.6.0.5"),sQuery(id+"F1.wireOp",EDGE,"E6.6.0.6"),sQuery(id+"F1.wireOp",EDGE,"E6.6.0.7"),sQuery(id+"F1.wireOp",EDGE,"E6.6.0.8"),sQuery(id+"F1.wireOp",EDGE,"E6.6.0.9"),sQuery(id+"F1.wireOp",EDGE,"E6.6.0.11"),sQuery(id+"F1.wireOp",EDGE,"E6.6.0.13"),sQuery(id+"F1.wireOp",EDGE,"E6.6.0.14"),sQuery(id+"F1.wireOp",EDGE,"E6.6.0.15"),sQuery(id+"F1.wireOp",EDGE,"E6.6.0.16"),sQuery(id+"F1.wireOp",EDGE,"E6.6.0.17"),sQuery(id+"F1.wireOp",EDGE,"E6.6.0.18"),sQuery(id+"F1.wireOp",EDGE,"E6.6.0.19"),sQuery(id+"F1.wireOp",EDGE,"E6.6.0.21"),sQuery(id+"F1.wireOp",EDGE,"E6.6.0.22"),sQuery(id+"F1.wireOp",EDGE,"E6.6.0.23"),sQuery(id+"F1.wireOp",EDGE,"E6.7.0.1"),sQuery(id+"F1.wireOp",EDGE,"E6.7.0.3"),sQuery(id+"F1.wireOp",EDGE,"E6.7.0.5"),sQuery(id+"F1.wireOp",EDGE,"E6.7.0.6"),sQuery(id+"F1.wireOp",EDGE,"E6.7.0.7"),sQuery(id+"F1.wireOp",EDGE,"E6.7.0.8"),sQuery(id+"F1.wireOp",EDGE,"E6.7.0.9"),sQuery(id+"F1.wireOp",EDGE,"E6.7.0.11"),sQuery(id+"F1.wireOp",EDGE,"E6.7.0.13"),sQuery(id+"F1.wireOp",EDGE,"E6.7.0.14"),sQuery(id+"F1.wireOp",EDGE,"E6.7.0.15"),sQuery(id+"F1.wireOp",EDGE,"E6.7.0.16"),sQuery(id+"F1.wireOp",EDGE,"E6.7.0.17"),sQuery(id+"F1.wireOp",EDGE,"E6.7.0.18"),sQuery(id+"F1.wireOp",EDGE,"E6.7.0.19"),sQuery(id+"F1.wireOp",EDGE,"E6.7.0.21"),sQuery(id+"F1.wireOp",EDGE,"E6.7.0.22"),sQuery(id+"F1.wireOp",EDGE,"E6.7.0.23"),sQuery(id+"F1.wireOp",EDGE,"E6.8.0.1"),sQuery(id+"F1.wireOp",EDGE,"E6.8.0.3"),sQuery(id+"F1.wireOp",EDGE,"E6.8.0.5"),sQuery(id+"F1.wireOp",EDGE,"E6.8.0.6"),sQuery(id+"F1.wireOp",EDGE,"E6.8.0.7"),sQuery(id+"F1.wireOp",EDGE,"E6.8.0.8"),sQuery(id+"F1.wireOp",EDGE,"E6.8.0.9"),sQuery(id+"F1.wireOp",EDGE,"E6.8.0.11"),sQuery(id+"F1.wireOp",EDGE,"E6.8.0.13"),sQuery(id+"F1.wireOp",EDGE,"E6.8.0.14"),sQuery(id+"F1.wireOp",EDGE,"E6.8.0.15"),sQuery(id+"F1.wireOp",EDGE,"E6.8.0.16"),sQuery(id+"F1.wireOp",EDGE,"E6.8.0.17"),sQuery(id+"F1.wireOp",EDGE,"E6.8.0.18"),sQuery(id+"F1.wireOp",EDGE,"E6.8.0.19"),sQuery(id+"F1.wireOp",EDGE,"E6.8.0.21"),sQuery(id+"F1.wireOp",EDGE,"E6.8.0.22"),sQuery(id+"F1.wireOp",EDGE,"E6.8.0.23"),sQuery(id+"F1.wireOp",EDGE,"E6.9.0.1"),sQuery(id+"F1.wireOp",EDGE,"E6.9.0.3"),sQuery(id+"F1.wireOp",EDGE,"E6.9.0.5"),sQuery(id+"F1.wireOp",EDGE,"E6.9.0.6"),sQuery(id+"F1.wireOp",EDGE,"E6.9.0.7"),sQuery(id+"F1.wireOp",EDGE,"E6.9.0.8"),sQuery(id+"F1.wireOp",EDGE,"E6.9.0.9"),sQuery(id+"F1.wireOp",EDGE,"E6.9.0.11"),sQuery(id+"F1.wireOp",EDGE,"E6.9.0.13"),sQuery(id+"F1.wireOp",EDGE,"E6.9.0.14"),sQuery(id+"F1.wireOp",EDGE,"E6.9.0.15"),sQuery(id+"F1.wireOp",EDGE,"E6.9.0.16"),sQuery(id+"F1.wireOp",EDGE,"E6.9.0.17"),sQuery(id+"F1.wireOp",EDGE,"E6.9.0.18"),sQuery(id+"F1.wireOp",EDGE,"E6.9.0.19"),sQuery(id+"F1.wireOp",EDGE,"E6.9.0.21"),sQuery(id+"F1.wireOp",EDGE,"E6.9.0.22"),sQuery(id+"F1.wireOp",EDGE,"E6.9.0.23"),sQuery(id+"F1.wireOp",EDGE,"E7.bottom"),sQuery(id+"F1.wireOp",EDGE,"E7.top"),sQuery(id+"F1.wireOp",EDGE,"E7.left"),sQuery(id+"F1.wireOp",EDGE,"E7.right"),sQuery(id+"F1.wireOp",EDGE,"E8.0"),sQuery(id+"F1.wireOp",EDGE,"E8.1"),sQuery(id+"F1.wireOp",EDGE,"E8.2"),sQuery(id+"F1.wireOp",EDGE,"E8.3"),sQuery(id+"F1.wireOp",EDGE,"E8.4"),sQuery(id+"F1.wireOp",EDGE,"E8.5")])],"isStart":false});
            chamfer(context, id + "F6", {"entities" : qUnion([Q0]), "width" : 0.66 * mm, "tangentPropagation" : true});
        }
        {
            var Q0;
            Q0=makeQuery(id+"F2.opExtrude","CAP_FACE",FACE,{"disambiguationData":[OSD([sQuery(id+"F1.wireOp",EDGE,"E0.0"),sQuery(id+"F1.wireOp",EDGE,"E0.1"),sQuery(id+"F1.wireOp",EDGE,"E0.2"),sQuery(id+"F1.wireOp",EDGE,"E0.3"),sQuery(id+"F1.wireOp",EDGE,"E0.4"),sQuery(id+"F1.wireOp",EDGE,"E0.5"),sQuery(id+"F1.wireOp",EDGE,"E1.0"),sQuery(id+"F1.wireOp",EDGE,"E1.1"),sQuery(id+"F1.wireOp",EDGE,"E1.2"),sQuery(id+"F1.wireOp",EDGE,"E1.3"),sQuery(id+"F1.wireOp",EDGE,"E1.4"),sQuery(id+"F1.wireOp",EDGE,"E1.5"),sQuery(id+"F1.wireOp",EDGE,"E5.0"),sQuery(id+"F1.wireOp",EDGE,"E5.1"),sQuery(id+"F1.wireOp",EDGE,"E5.2"),sQuery(id+"F1.wireOp",EDGE,"E5.3"),sQuery(id+"F1.wireOp",EDGE,"E5.4"),sQuery(id+"F1.wireOp",EDGE,"E5.5"),sQuery(id+"F1.wireOp",EDGE,"E6.1.0.1"),sQuery(id+"F1.wireOp",EDGE,"E6.1.0.3"),sQuery(id+"F1.wireOp",EDGE,"E6.1.0.5"),sQuery(id+"F1.wireOp",EDGE,"E6.1.0.6"),sQuery(id+"F1.wireOp",EDGE,"E6.1.0.7"),sQuery(id+"F1.wireOp",EDGE,"E6.1.0.8"),sQuery(id+"F1.wireOp",EDGE,"E6.1.0.9"),sQuery(id+"F1.wireOp",EDGE,"E6.1.0.11"),sQuery(id+"F1.wireOp",EDGE,"E6.1.0.13"),sQuery(id+"F1.wireOp",EDGE,"E6.1.0.14"),sQuery(id+"F1.wireOp",EDGE,"E6.1.0.15"),sQuery(id+"F1.wireOp",EDGE,"E6.1.0.16"),sQuery(id+"F1.wireOp",EDGE,"E6.1.0.17"),sQuery(id+"F1.wireOp",EDGE,"E6.1.0.18"),sQuery(id+"F1.wireOp",EDGE,"E6.1.0.19"),sQuery(id+"F1.wireOp",EDGE,"E6.1.0.21"),sQuery(id+"F1.wireOp",EDGE,"E6.1.0.22"),sQuery(id+"F1.wireOp",EDGE,"E6.1.0.23"),sQuery(id+"F1.wireOp",EDGE,"E6.2.0.1"),sQuery(id+"F1.wireOp",EDGE,"E6.2.0.3"),sQuery(id+"F1.wireOp",EDGE,"E6.2.0.5"),sQuery(id+"F1.wireOp",EDGE,"E6.2.0.6"),sQuery(id+"F1.wireOp",EDGE,"E6.2.0.7"),sQuery(id+"F1.wireOp",EDGE,"E6.2.0.8"),sQuery(id+"F1.wireOp",EDGE,"E6.2.0.9"),sQuery(id+"F1.wireOp",EDGE,"E6.2.0.11"),sQuery(id+"F1.wireOp",EDGE,"E6.2.0.13"),sQuery(id+"F1.wireOp",EDGE,"E6.2.0.14"),sQuery(id+"F1.wireOp",EDGE,"E6.2.0.15"),sQuery(id+"F1.wireOp",EDGE,"E6.2.0.16"),sQuery(id+"F1.wireOp",EDGE,"E6.2.0.17"),sQuery(id+"F1.wireOp",EDGE,"E6.2.0.18"),sQuery(id+"F1.wireOp",EDGE,"E6.2.0.19"),sQuery(id+"F1.wireOp",EDGE,"E6.2.0.21"),sQuery(id+"F1.wireOp",EDGE,"E6.2.0.22"),sQuery(id+"F1.wireOp",EDGE,"E6.2.0.23"),sQuery(id+"F1.wireOp",EDGE,"E6.3.0.1"),sQuery(id+"F1.wireOp",EDGE,"E6.3.0.3"),sQuery(id+"F1.wireOp",EDGE,"E6.3.0.5"),sQuery(id+"F1.wireOp",EDGE,"E6.3.0.6"),sQuery(id+"F1.wireOp",EDGE,"E6.3.0.7"),sQuery(id+"F1.wireOp",EDGE,"E6.3.0.8"),sQuery(id+"F1.wireOp",EDGE,"E6.3.0.9"),sQuery(id+"F1.wireOp",EDGE,"E6.3.0.11"),sQuery(id+"F1.wireOp",EDGE,"E6.3.0.13"),sQuery(id+"F1.wireOp",EDGE,"E6.3.0.14"),sQuery(id+"F1.wireOp",EDGE,"E6.3.0.15"),sQuery(id+"F1.wireOp",EDGE,"E6.3.0.16"),sQuery(id+"F1.wireOp",EDGE,"E6.3.0.17"),sQuery(id+"F1.wireOp",EDGE,"E6.3.0.18"),sQuery(id+"F1.wireOp",EDGE,"E6.3.0.19"),sQuery(id+"F1.wireOp",EDGE,"E6.3.0.21"),sQuery(id+"F1.wireOp",EDGE,"E6.3.0.22"),sQuery(id+"F1.wireOp",EDGE,"E6.3.0.23"),sQuery(id+"F1.wireOp",EDGE,"E6.4.0.1"),sQuery(id+"F1.wireOp",EDGE,"E6.4.0.3"),sQuery(id+"F1.wireOp",EDGE,"E6.4.0.5"),sQuery(id+"F1.wireOp",EDGE,"E6.4.0.6"),sQuery(id+"F1.wireOp",EDGE,"E6.4.0.7"),sQuery(id+"F1.wireOp",EDGE,"E6.4.0.8"),sQuery(id+"F1.wireOp",EDGE,"E6.4.0.9"),sQuery(id+"F1.wireOp",EDGE,"E6.4.0.11"),sQuery(id+"F1.wireOp",EDGE,"E6.4.0.13"),sQuery(id+"F1.wireOp",EDGE,"E6.4.0.14"),sQuery(id+"F1.wireOp",EDGE,"E6.4.0.15"),sQuery(id+"F1.wireOp",EDGE,"E6.4.0.16"),sQuery(id+"F1.wireOp",EDGE,"E6.4.0.17"),sQuery(id+"F1.wireOp",EDGE,"E6.4.0.18"),sQuery(id+"F1.wireOp",EDGE,"E6.4.0.19"),sQuery(id+"F1.wireOp",EDGE,"E6.4.0.21"),sQuery(id+"F1.wireOp",EDGE,"E6.4.0.22"),sQuery(id+"F1.wireOp",EDGE,"E6.4.0.23"),sQuery(id+"F1.wireOp",EDGE,"E6.5.0.1"),sQuery(id+"F1.wireOp",EDGE,"E6.5.0.3"),sQuery(id+"F1.wireOp",EDGE,"E6.5.0.5"),sQuery(id+"F1.wireOp",EDGE,"E6.5.0.6"),sQuery(id+"F1.wireOp",EDGE,"E6.5.0.7"),sQuery(id+"F1.wireOp",EDGE,"E6.5.0.8"),sQuery(id+"F1.wireOp",EDGE,"E6.5.0.9"),sQuery(id+"F1.wireOp",EDGE,"E6.5.0.11"),sQuery(id+"F1.wireOp",EDGE,"E6.5.0.13"),sQuery(id+"F1.wireOp",EDGE,"E6.5.0.14"),sQuery(id+"F1.wireOp",EDGE,"E6.5.0.15"),sQuery(id+"F1.wireOp",EDGE,"E6.5.0.16"),sQuery(id+"F1.wireOp",EDGE,"E6.5.0.17"),sQuery(id+"F1.wireOp",EDGE,"E6.5.0.18"),sQuery(id+"F1.wireOp",EDGE,"E6.5.0.19"),sQuery(id+"F1.wireOp",EDGE,"E6.5.0.21"),sQuery(id+"F1.wireOp",EDGE,"E6.5.0.22"),sQuery(id+"F1.wireOp",EDGE,"E6.5.0.23"),sQuery(id+"F1.wireOp",EDGE,"E6.6.0.1"),sQuery(id+"F1.wireOp",EDGE,"E6.6.0.3"),sQuery(id+"F1.wireOp",EDGE,"E6.6.0.5"),sQuery(id+"F1.wireOp",EDGE,"E6.6.0.6"),sQuery(id+"F1.wireOp",EDGE,"E6.6.0.7"),sQuery(id+"F1.wireOp",EDGE,"E6.6.0.8"),sQuery(id+"F1.wireOp",EDGE,"E6.6.0.9"),sQuery(id+"F1.wireOp",EDGE,"E6.6.0.11"),sQuery(id+"F1.wireOp",EDGE,"E6.6.0.13"),sQuery(id+"F1.wireOp",EDGE,"E6.6.0.14"),sQuery(id+"F1.wireOp",EDGE,"E6.6.0.15"),sQuery(id+"F1.wireOp",EDGE,"E6.6.0.16"),sQuery(id+"F1.wireOp",EDGE,"E6.6.0.17"),sQuery(id+"F1.wireOp",EDGE,"E6.6.0.18"),sQuery(id+"F1.wireOp",EDGE,"E6.6.0.19"),sQuery(id+"F1.wireOp",EDGE,"E6.6.0.21"),sQuery(id+"F1.wireOp",EDGE,"E6.6.0.22"),sQuery(id+"F1.wireOp",EDGE,"E6.6.0.23"),sQuery(id+"F1.wireOp",EDGE,"E6.7.0.1"),sQuery(id+"F1.wireOp",EDGE,"E6.7.0.3"),sQuery(id+"F1.wireOp",EDGE,"E6.7.0.5"),sQuery(id+"F1.wireOp",EDGE,"E6.7.0.6"),sQuery(id+"F1.wireOp",EDGE,"E6.7.0.7"),sQuery(id+"F1.wireOp",EDGE,"E6.7.0.8"),sQuery(id+"F1.wireOp",EDGE,"E6.7.0.9"),sQuery(id+"F1.wireOp",EDGE,"E6.7.0.11"),sQuery(id+"F1.wireOp",EDGE,"E6.7.0.13"),sQuery(id+"F1.wireOp",EDGE,"E6.7.0.14"),sQuery(id+"F1.wireOp",EDGE,"E6.7.0.15"),sQuery(id+"F1.wireOp",EDGE,"E6.7.0.16"),sQuery(id+"F1.wireOp",EDGE,"E6.7.0.17"),sQuery(id+"F1.wireOp",EDGE,"E6.7.0.18"),sQuery(id+"F1.wireOp",EDGE,"E6.7.0.19"),sQuery(id+"F1.wireOp",EDGE,"E6.7.0.21"),sQuery(id+"F1.wireOp",EDGE,"E6.7.0.22"),sQuery(id+"F1.wireOp",EDGE,"E6.7.0.23"),sQuery(id+"F1.wireOp",EDGE,"E6.8.0.1"),sQuery(id+"F1.wireOp",EDGE,"E6.8.0.3"),sQuery(id+"F1.wireOp",EDGE,"E6.8.0.5"),sQuery(id+"F1.wireOp",EDGE,"E6.8.0.6"),sQuery(id+"F1.wireOp",EDGE,"E6.8.0.7"),sQuery(id+"F1.wireOp",EDGE,"E6.8.0.8"),sQuery(id+"F1.wireOp",EDGE,"E6.8.0.9"),sQuery(id+"F1.wireOp",EDGE,"E6.8.0.11"),sQuery(id+"F1.wireOp",EDGE,"E6.8.0.13"),sQuery(id+"F1.wireOp",EDGE,"E6.8.0.14"),sQuery(id+"F1.wireOp",EDGE,"E6.8.0.15"),sQuery(id+"F1.wireOp",EDGE,"E6.8.0.16"),sQuery(id+"F1.wireOp",EDGE,"E6.8.0.17"),sQuery(id+"F1.wireOp",EDGE,"E6.8.0.18"),sQuery(id+"F1.wireOp",EDGE,"E6.8.0.19"),sQuery(id+"F1.wireOp",EDGE,"E6.8.0.21"),sQuery(id+"F1.wireOp",EDGE,"E6.8.0.22"),sQuery(id+"F1.wireOp",EDGE,"E6.8.0.23"),sQuery(id+"F1.wireOp",EDGE,"E6.9.0.1"),sQuery(id+"F1.wireOp",EDGE,"E6.9.0.3"),sQuery(id+"F1.wireOp",EDGE,"E6.9.0.5"),sQuery(id+"F1.wireOp",EDGE,"E6.9.0.6"),sQuery(id+"F1.wireOp",EDGE,"E6.9.0.7"),sQuery(id+"F1.wireOp",EDGE,"E6.9.0.8"),sQuery(id+"F1.wireOp",EDGE,"E6.9.0.9"),sQuery(id+"F1.wireOp",EDGE,"E6.9.0.11"),sQuery(id+"F1.wireOp",EDGE,"E6.9.0.13"),sQuery(id+"F1.wireOp",EDGE,"E6.9.0.14"),sQuery(id+"F1.wireOp",EDGE,"E6.9.0.15"),sQuery(id+"F1.wireOp",EDGE,"E6.9.0.16"),sQuery(id+"F1.wireOp",EDGE,"E6.9.0.17"),sQuery(id+"F1.wireOp",EDGE,"E6.9.0.18"),sQuery(id+"F1.wireOp",EDGE,"E6.9.0.19"),sQuery(id+"F1.wireOp",EDGE,"E6.9.0.21"),sQuery(id+"F1.wireOp",EDGE,"E6.9.0.22"),sQuery(id+"F1.wireOp",EDGE,"E6.9.0.23"),sQuery(id+"F1.wireOp",EDGE,"E7.bottom"),sQuery(id+"F1.wireOp",EDGE,"E7.top"),sQuery(id+"F1.wireOp",EDGE,"E7.left"),sQuery(id+"F1.wireOp",EDGE,"E7.right"),sQuery(id+"F1.wireOp",EDGE,"E8.0"),sQuery(id+"F1.wireOp",EDGE,"E8.1"),sQuery(id+"F1.wireOp",EDGE,"E8.2"),sQuery(id+"F1.wireOp",EDGE,"E8.3"),sQuery(id+"F1.wireOp",EDGE,"E8.4"),sQuery(id+"F1.wireOp",EDGE,"E8.5")])],"isStart":false});
            var sketch = newSketch(context, id + "F7", { "sketchPlane" : qUnion([Q0])});
            skPoint(sketch, "E14.oppositeSnap0", {"position": v(8.5, -2.91) * mm});
            skLineSegment(sketch, "E14.bottom", {"start": v(-14.5, 15.06) * mm, "end": v(8.5, 15.06) * mm});
            skLineSegment(sketch, "E14.top", {"start": v(-14.5, -6.57) * mm, "end": v(8.5, -6.57) * mm});
            skLineSegment(sketch, "E14.left", {"start": v(-14.5, 15.06) * mm, "end": v(-14.5, -6.57) * mm});
            skLineSegment(sketch, "E14.right", {"start": v(8.5, 15.06) * mm, "end": v(8.5, -6.57) * mm});
            skSolve(sketch);
        }
        {
            var Q0;
            Q0 = qSketchRegion(id + "F7", true);
            extrude(context, id + "F8", {"entities" : qUnion([Q0]), "operationType" : NewBodyOperationType.INTERSECT, "endBound" : BoundingType.THROUGH_ALL, "oppositeDirection" : true, "depth" : 25 * mm});
        }
    });
